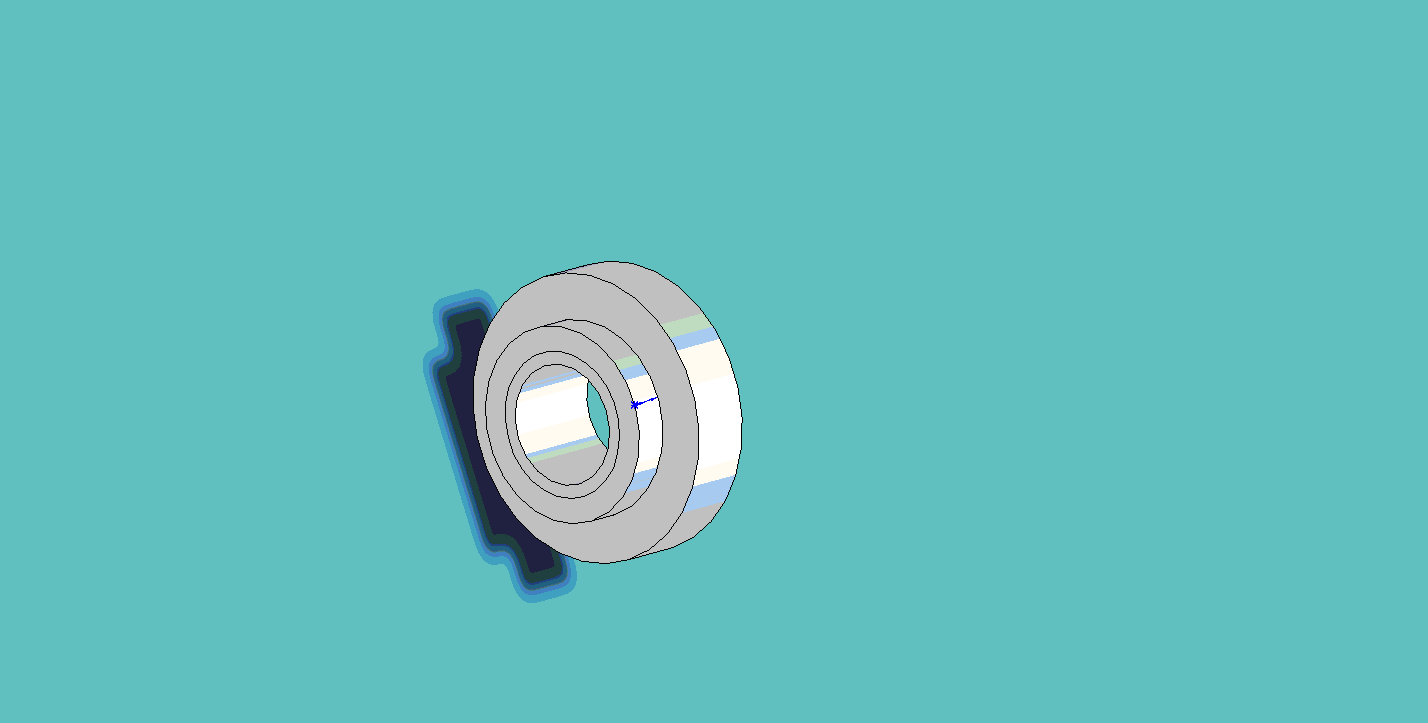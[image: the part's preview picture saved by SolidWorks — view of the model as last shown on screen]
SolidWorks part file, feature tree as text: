
SOLIDWORKS PART (.sldprt)
format: sldprt  version: not decoded by parser v0  size: 100,864 bytes
history: native  units: mm
features: plane x3, sketch x3, material x1, revolve x1, hole x1, thread x1, chamfer x1 (+10 scaffold rows collapsed)
feature tree (21):
  scaffold x10  (default folders/planes/origin — collapsed)
  material  "Matériau <non spécifié>"
  plane  "Plan de face"
  plane  "Plan de dessus"
  plane  "Plan de droite"
  sketch  "Esquisse1"  dims[D1=2.0mm D2=7.9mm D3=0.98mm D4=5.38mm]
  revolve  "Révolution1"  Angle=360deg
  hole  "Trou taraudé M4x0.71"  Diameter=3.3mm Depth=2.98mm
  sketch  "Esquisse3D1"
  sketch  "Esquisse2"  dims[hole-wizard template sketch: 59 standard entries collapsed; hole parameters kept: c18.Diamètre du trou pour taraudage jusqu'au prochain=3.3mm c18.Profondeur du trou pour taraudage jusqu'au prochain=2.98mm]
  thread  "Filetage de perçage1"  Diameter=4mm  [1 undecoded]
  chamfer  "Chanfrein1"  Distance=0.2mm Angle=45deg
decode coverage: 6 of 7 modeling features carry decoded parameters
note: ~ marks probable driven/reference dimensions
note: 1 parameter value undecoded
note: suppression state not decoded; provenance and decode notes live in map.json
